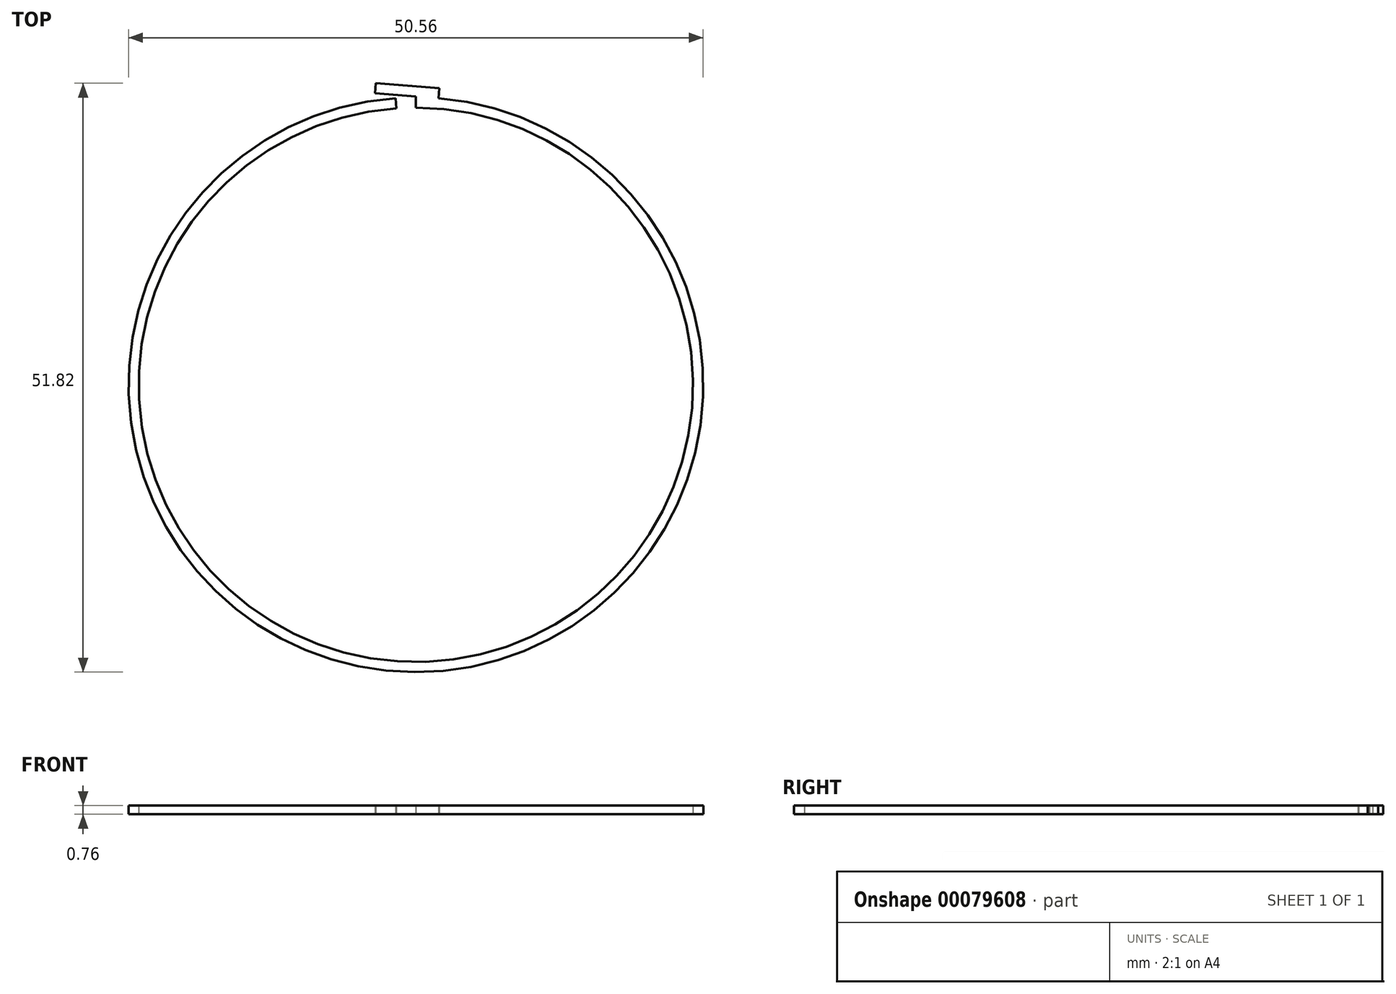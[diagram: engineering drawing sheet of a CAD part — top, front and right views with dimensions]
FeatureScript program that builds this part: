
annotation { "Feature Type Name" : "Feature", "Feature Type Description" : "" }
export const myFeature = defineFeature(function(context is Context, id is Id, definition is map)
    precondition{}
    {
        {
            var Q0;
            Q0=qCreatedBy(makeId("Top.planeOp"),FACE);
            var sketch = newSketch(context, id + "F0", { "sketchPlane" : qUnion([Q0])});
            skArc(sketch, "E0", {"start": v(-1.7, 24.32) * mm, "mid": v(0.85, -24.37) * mm, "end": v(0, 24.38) * mm});
            skArc(sketch, "E1", {"start": v(-1.77, 25.22) * mm, "mid": v(-0.1, -25.28) * mm, "end": v(1.99, 25.2) * mm});
            skLineSegment(sketch, "E2", {"start": v(-1.7, 24.32) * mm, "end": v(-1.77, 25.22) * mm});
            skLineSegment(sketch, "E3", {"start": v(2.06, 26.1) * mm, "end": v(1.99, 25.2) * mm});
            skLineSegment(sketch, "E4", {"start": v(2.06, 26.1) * mm, "end": v(-3.53, 26.54) * mm});
            skLineSegment(sketch, "E5", {"start": v(0, 25.36) * mm, "end": v(-3.6, 25.65) * mm});
            skLineSegment(sketch, "E6", {"start": v(-3.6, 25.65) * mm, "end": v(-3.53, 26.54) * mm});
            skPoint(sketch, "E7.start.orphan", {"position": v(0, 25.28) * mm});
            skLineSegment(sketch, "E8", {"start": v(0, 24.38) * mm, "end": v(0, 25.36) * mm});
            skSolve(sketch);
        }
        {
            var Q0;
            Q0 = qSketchRegion(id + "F0", true);
            extrude(context, id + "F1", {"entities" : qUnion([Q0]), "depth" : 0.76 * mm});
        }
    });
